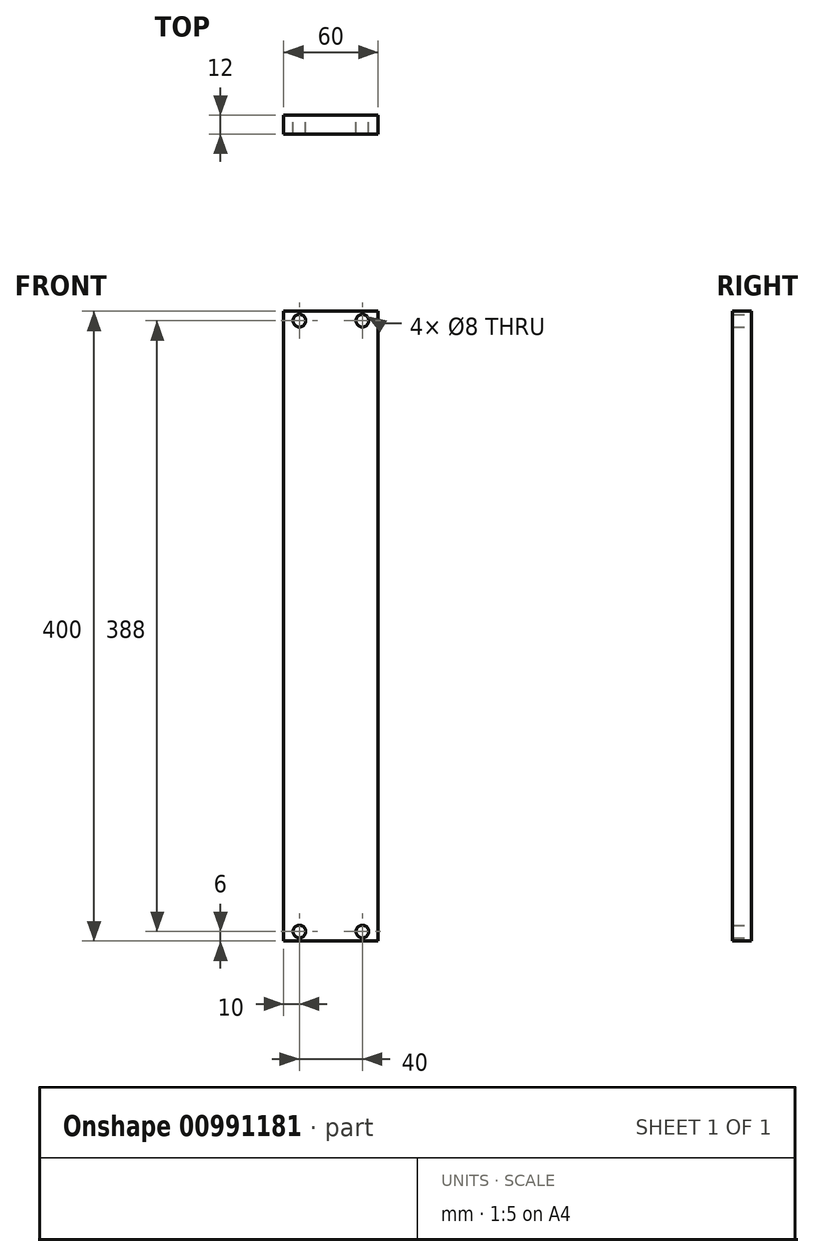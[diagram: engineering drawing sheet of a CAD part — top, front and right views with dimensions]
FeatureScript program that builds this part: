
annotation { "Feature Type Name" : "Feature", "Feature Type Description" : "" }
export const myFeature = defineFeature(function(context is Context, id is Id, definition is map)
    precondition{}
    {
        {
            var Q0;
            Q0=qCreatedBy(makeId("Front.planeOp"),FACE);
            var sketch = newSketch(context, id + "F0", { "sketchPlane" : qUnion([Q0])});
            skLineSegment(sketch, "E0.bottom", {"start": v(0, 0) * mm, "end": v(60, 0) * mm});
            skLineSegment(sketch, "E0.top", {"start": v(0, 400) * mm, "end": v(60, 400) * mm});
            skLineSegment(sketch, "E0.left", {"start": v(0, 0) * mm, "end": v(0, 400) * mm});
            skLineSegment(sketch, "E0.right", {"start": v(60, 0) * mm, "end": v(60, 400) * mm});
            skCircle(sketch, "E1", {"center": v(10, 6) * mm, "radius": 4 * mm});
            skCircle(sketch, "E2", {"center": v(50, 6) * mm, "radius": 4 * mm});
            skCircle(sketch, "E3", {"center": v(10, 394) * mm, "radius": 4 * mm});
            skCircle(sketch, "E4", {"center": v(50, 394) * mm, "radius": 4 * mm});
            skSolve(sketch);
        }
        {
            var Q0;
            Q0 = qSketchRegion(id + "F0", true);
            extrude(context, id + "F1", {"entities" : qUnion([Q0]), "depth" : 12 * mm, "offsetDistance" : 25 * mm});
        }
    });
